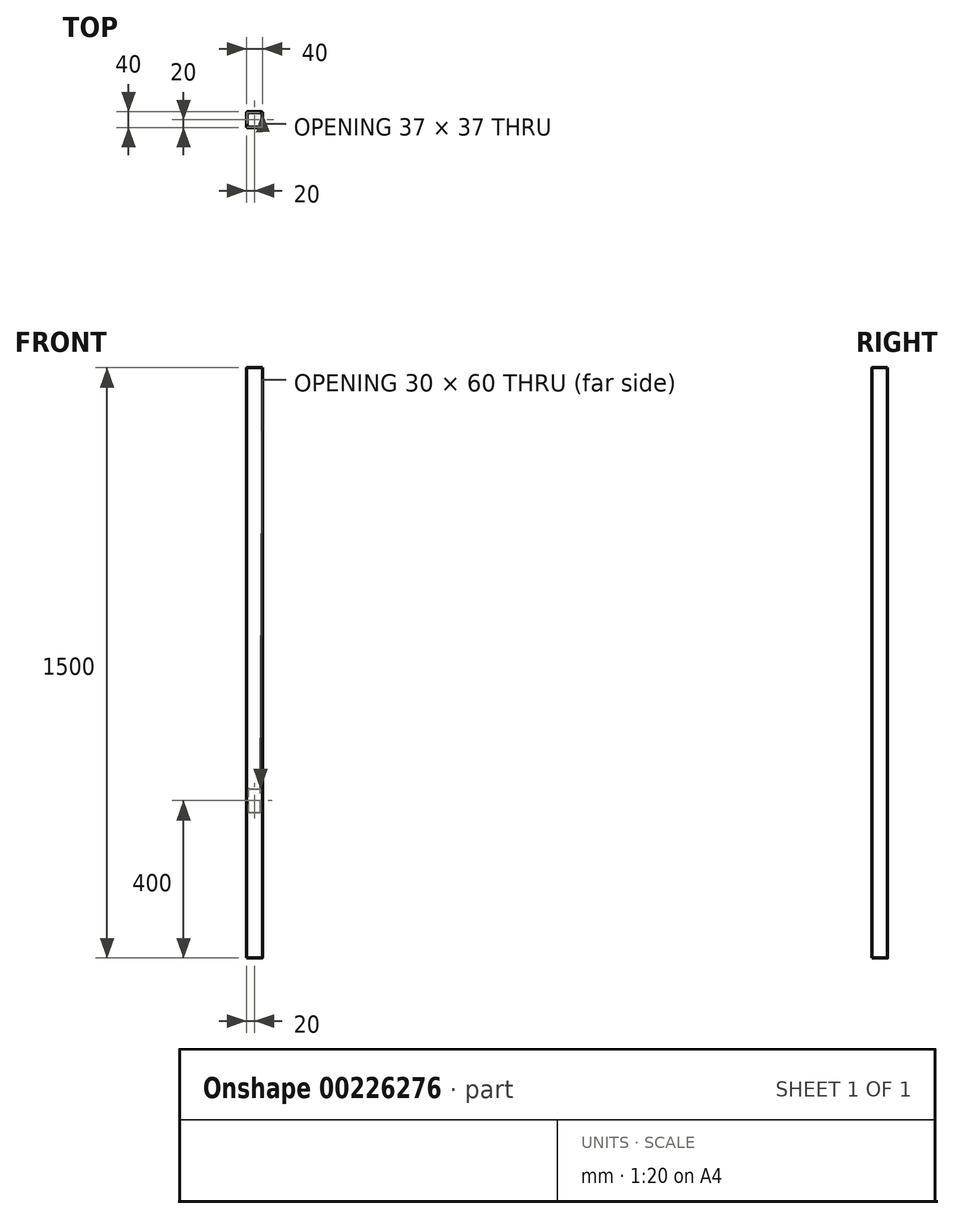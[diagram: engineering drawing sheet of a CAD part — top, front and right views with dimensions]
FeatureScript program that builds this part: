
annotation { "Feature Type Name" : "Feature", "Feature Type Description" : "" }
export const myFeature = defineFeature(function(context is Context, id is Id, definition is map)
    precondition{}
    {
        {
            var Q0;
            Q0=qCreatedBy(makeId("Top.planeOp"),FACE);
            var sketch = newSketch(context, id + "F0", { "sketchPlane" : qUnion([Q0])});
            skLineSegment(sketch, "E0.bottom", {"start": v(18, 20) * mm, "end": v(-18, 20) * mm});
            skLineSegment(sketch, "E0.top", {"start": v(18, -20) * mm, "end": v(-18, -20) * mm});
            skLineSegment(sketch, "E0.left", {"start": v(20, 18) * mm, "end": v(20, -18) * mm});
            skLineSegment(sketch, "E0.right", {"start": v(-20, 18) * mm, "end": v(-20, -18) * mm});
            skPoint(sketch, "E0.middle", {"position": v(0, 0) * mm});
            skPoint(sketch, "E1.visualSharp", {"position": v(-20, 20) * mm});
            skArc(sketch, "E1.filletArc", {"start": v(-18, 20) * mm, "mid": v(-19.41, 19.41) * mm, "end": v(-20, 18) * mm});
            skPoint(sketch, "E2.visualSharp", {"position": v(-20, -20) * mm});
            skArc(sketch, "E2.filletArc", {"start": v(-20, -18) * mm, "mid": v(-19.41, -19.41) * mm, "end": v(-18, -20) * mm});
            skPoint(sketch, "E3.visualSharp", {"position": v(20, -20) * mm});
            skArc(sketch, "E3.filletArc", {"start": v(18, -20) * mm, "mid": v(19.41, -19.41) * mm, "end": v(20, -18) * mm});
            skPoint(sketch, "E4.visualSharp", {"position": v(20, 20) * mm});
            skArc(sketch, "E4.filletArc", {"start": v(20, 18) * mm, "mid": v(19.41, 19.41) * mm, "end": v(18, 20) * mm});
            skLineSegment(sketch, "E5.bottom", {"start": v(17.5, 18.5) * mm, "end": v(-18.5, 18.5) * mm});
            skLineSegment(sketch, "E5.top", {"start": v(17.5, -18.5) * mm, "end": v(-17.5, -18.5) * mm});
            skLineSegment(sketch, "E5.left", {"start": v(18.5, 17.5) * mm, "end": v(18.5, -17.5) * mm});
            skLineSegment(sketch, "E5.right", {"start": v(-18.5, 18.5) * mm, "end": v(-18.5, -17.5) * mm});
            skPoint(sketch, "E6.visualSharp", {"position": v(18.5, 18.5) * mm});
            skArc(sketch, "E6.filletArc", {"start": v(18.5, 17.5) * mm, "mid": v(18.2, 18.2) * mm, "end": v(17.5, 18.5) * mm});
            skPoint(sketch, "E7.visualSharp", {"position": v(18.5, -18.5) * mm});
            skArc(sketch, "E7.filletArc", {"start": v(17.5, -18.5) * mm, "mid": v(18.2, -18.2) * mm, "end": v(18.5, -17.5) * mm});
            skPoint(sketch, "E8.visualSharp", {"position": v(-18.5, -18.5) * mm});
            skArc(sketch, "E8.filletArc", {"start": v(-18.5, -17.5) * mm, "mid": v(-18.2, -18.2) * mm, "end": v(-17.5, -18.5) * mm});
            skSolve(sketch);
        }
        {
            var Q0;
            Q0=makeQuery(id+"F0.imprint","IMPRINT",FACE,{"disambiguationData":[TD([[makeQuery(id+"F0.imprint","IMPRINT",EDGE,{"derivedFrom":sQuery(id+"F0.wireOp",EDGE,"E0.bottom")}),1.0]])]});
            extrude(context, id + "F1", {"entities" : qUnion([Q0]), "depth" : 1500 * mm});
        }
        {
            var Q0;
            Q0=makeQuery(id+"F1.opExtrude","SWEPT_FACE",FACE,{"disambiguationData":[OSD([sQuery(id+"F0.wireOp",EDGE,"E0.bottom")])]});
            var sketch = newSketch(context, id + "F2", { "sketchPlane" : qUnion([Q0])});
            skLineSegment(sketch, "E9.bottom", {"start": v(13, 370) * mm, "end": v(-13, 370) * mm});
            skLineSegment(sketch, "E9.top", {"start": v(13, 430) * mm, "end": v(-13, 430) * mm});
            skLineSegment(sketch, "E9.left", {"start": v(15, 372) * mm, "end": v(15, 428) * mm});
            skLineSegment(sketch, "E9.right", {"start": v(-15, 372) * mm, "end": v(-15, 428) * mm});
            skPoint(sketch, "E9.middle", {"position": v(0, 400) * mm});
            skPoint(sketch, "E10.visualSharp", {"position": v(-15, 430) * mm});
            skArc(sketch, "E10.filletArc", {"start": v(-13, 430) * mm, "mid": v(-14.41, 429.41) * mm, "end": v(-15, 428) * mm});
            skPoint(sketch, "E11.visualSharp", {"position": v(15, 430) * mm});
            skArc(sketch, "E11.filletArc", {"start": v(15, 428) * mm, "mid": v(14.41, 429.41) * mm, "end": v(13, 430) * mm});
            skPoint(sketch, "E12.visualSharp", {"position": v(15, 370) * mm});
            skArc(sketch, "E12.filletArc", {"start": v(13, 370) * mm, "mid": v(14.41, 370.59) * mm, "end": v(15, 372) * mm});
            skPoint(sketch, "E13.visualSharp", {"position": v(-15, 370) * mm});
            skArc(sketch, "E13.filletArc", {"start": v(-15, 372) * mm, "mid": v(-14.41, 370.59) * mm, "end": v(-13, 370) * mm});
            skSolve(sketch);
        }
        {
            var Q0;
            Q0=makeQuery(id+"F2.imprint","IMPRINT",FACE,{"disambiguationData":[TD([[makeQuery(id+"F2.imprint","IMPRINT",EDGE,{"derivedFrom":sQuery(id+"F2.wireOp",EDGE,"E9.bottom")}),-1.0]])]});
            extrude(context, id + "F3", {"entities" : qUnion([Q0]), "operationType" : NewBodyOperationType.REMOVE, "oppositeDirection" : true, "depth" : 25 * mm});
        }
    });
